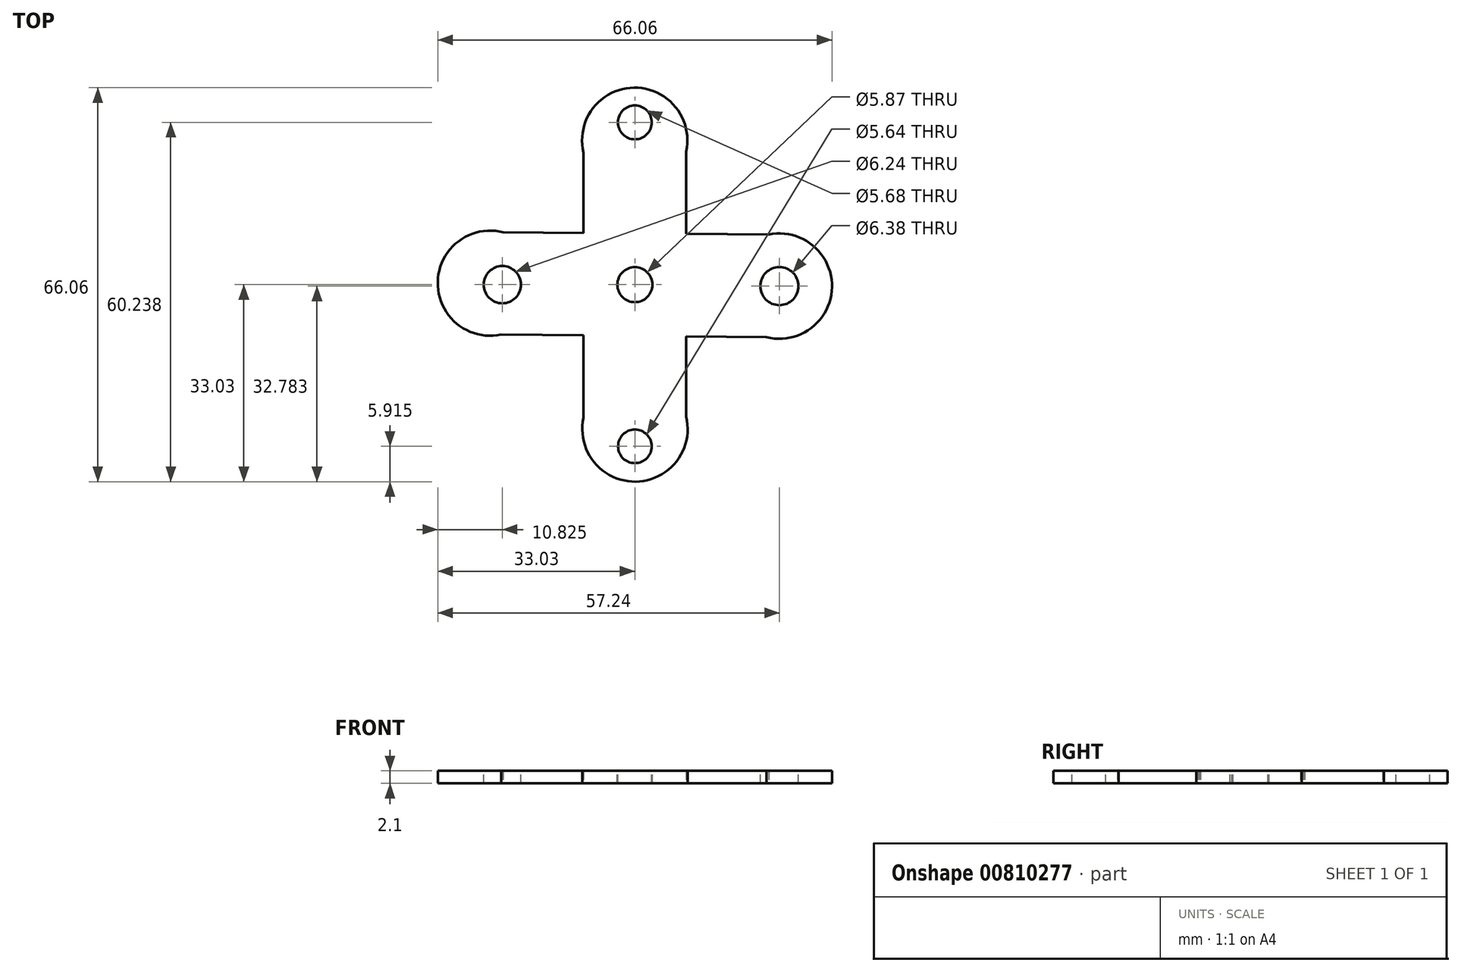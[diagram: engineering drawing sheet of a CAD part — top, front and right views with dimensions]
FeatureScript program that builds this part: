
annotation { "Feature Type Name" : "Feature", "Feature Type Description" : "" }
export const myFeature = defineFeature(function(context is Context, id is Id, definition is map)
    precondition{}
    {
        {
            var Q0;
            Q0=qCreatedBy(makeId("Top.planeOp"),FACE);
            var sketch = newSketch(context, id + "F0", { "sketchPlane" : qUnion([Q0])});
            skLineSegment(sketch, "E0", {"start": v(0, 0) * mm, "end": v(0, 75.49) * mm});
            skLineSegment(sketch, "E1", {"start": v(0, 0) * mm, "end": v(-75, -74.3) * mm});
            skLineSegment(sketch, "E2", {"start": v(0, 0) * mm, "end": v(74.3, -75) * mm});
            skArc(sketch, "E3", {"start": v(8.6, 22.33) * mm, "mid": v(-0.12, 33.03) * mm, "end": v(-8.6, 22.13) * mm});
            skLineSegment(sketch, "E4", {"start": v(-8.6, 22.13) * mm, "end": v(-8.6, -8.52) * mm});
            skLineSegment(sketch, "E5", {"start": v(8.6, 22.33) * mm, "end": v(8.6, -8.68) * mm});
            skLineSegment(sketch, "E6.MirrorCS", {"start": v(-22.4, -8.39) * mm, "end": v(8.6, -8.68) * mm});
            skArc(sketch, "E7.MirrorCS", {"start": v(-22.4, -8.39) * mm, "mid": v(-33.03, 0.43) * mm, "end": v(-22.05, 8.8) * mm});
            skLineSegment(sketch, "E8.MirrorCS", {"start": v(-22.05, 8.8) * mm, "end": v(8.6, 8.52) * mm});
            skLineSegment(sketch, "E9.MirrorCS", {"start": v(-8.6, -22.33) * mm, "end": v(-8.6, 8.68) * mm});
            skArc(sketch, "E10.MirrorCS", {"start": v(-8.6, -22.33) * mm, "mid": v(0.12, -33.03) * mm, "end": v(8.6, -22.13) * mm});
            skLineSegment(sketch, "E11.MirrorCS", {"start": v(8.6, -22.13) * mm, "end": v(8.6, 8.52) * mm});
            skLineSegment(sketch, "E12.MirrorCS", {"start": v(22.05, -8.8) * mm, "end": v(-8.6, -8.52) * mm});
            skArc(sketch, "E13.MirrorCS", {"start": v(22.4, 8.39) * mm, "mid": v(33.03, -0.43) * mm, "end": v(22.05, -8.8) * mm});
            skLineSegment(sketch, "E14.MirrorCS", {"start": v(22.4, 8.39) * mm, "end": v(-8.6, 8.68) * mm});
            skSolve(sketch);
        }
        {
            var Q0;
            Q0 = qSketchRegion(id + "F0", true);
            extrude(context, id + "F1", {"entities" : qUnion([Q0]), "depth" : 2.1 * mm, "offsetDistance" : 25 * mm});
        }
        {
            var Q0;
            Q0=makeQuery(id+"F1.opExtrude","CAP_FACE",FACE,{"disambiguationData":[OSD([sQuery(id+"F0.wireOp",EDGE,"E3"),sQuery(id+"F0.wireOp",EDGE,"E4"),sQuery(id+"F0.wireOp",EDGE,"E5"),sQuery(id+"F0.wireOp",EDGE,"E6.MirrorCS"),sQuery(id+"F0.wireOp",EDGE,"E9.MirrorCS"),sQuery(id+"F0.wireOp",EDGE,"E10.MirrorCS"),sQuery(id+"F0.wireOp",EDGE,"E11.MirrorCS"),sQuery(id+"F0.wireOp",EDGE,"E8.MirrorCS"),sQuery(id+"F0.wireOp",EDGE,"E7.MirrorCS"),sQuery(id+"F0.wireOp",EDGE,"E12.MirrorCS"),sQuery(id+"F0.wireOp",EDGE,"E13.MirrorCS"),sQuery(id+"F0.wireOp",EDGE,"E14.MirrorCS")])],"isStart":false});
            var sketch = newSketch(context, id + "F2", { "sketchPlane" : qUnion([Q0])});
            skCircle(sketch, "E15", {"center": v(0, 0) * mm, "radius": 2.94 * mm});
            skCircle(sketch, "E16", {"center": v(24.21, -0.25) * mm, "radius": 3.2 * mm});
            skCircle(sketch, "E17", {"center": v(0, 27.2) * mm, "radius": 2.84 * mm});
            skCircle(sketch, "E18", {"center": v(-22.2, 0) * mm, "radius": 3.12 * mm});
            skCircle(sketch, "E19", {"center": v(0, -27.12) * mm, "radius": 2.82 * mm});
            skSolve(sketch);
        }
        {
            var Q0;
            Q0 = qSketchRegion(id + "F2", true);
            extrude(context, id + "F3", {"entities" : qUnion([Q0]), "operationType" : NewBodyOperationType.REMOVE, "oppositeDirection" : true, "depth" : 25 * mm, "offsetDistance" : 25 * mm});
        }
    });
